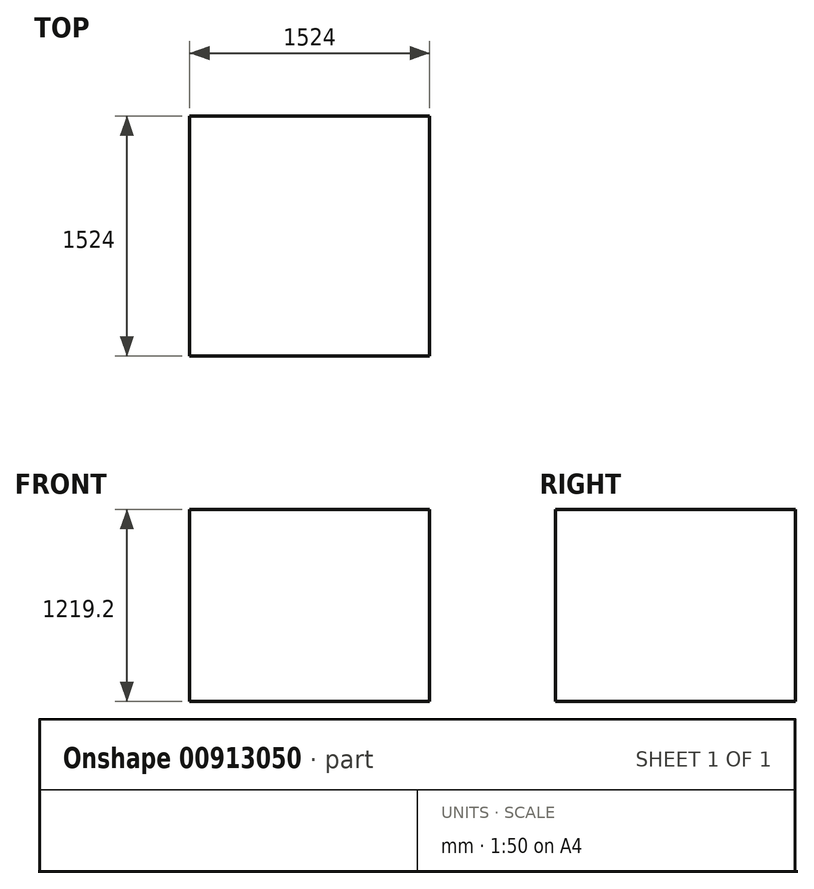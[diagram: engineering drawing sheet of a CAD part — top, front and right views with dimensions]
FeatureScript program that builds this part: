
annotation { "Feature Type Name" : "Feature", "Feature Type Description" : "" }
export const myFeature = defineFeature(function(context is Context, id is Id, definition is map)
    precondition{}
    {
        {
            var Q0;
            Q0=qCreatedBy(makeId("Top.planeOp"),FACE);
            var sketch = newSketch(context, id + "F0", { "sketchPlane" : qUnion([Q0])});
            skLineSegment(sketch, "E0.bottom", {"start": v(762, -762) * mm, "end": v(-762, -762) * mm});
            skLineSegment(sketch, "E0.top", {"start": v(762, 762) * mm, "end": v(-762, 762) * mm});
            skLineSegment(sketch, "E0.left", {"start": v(762, -762) * mm, "end": v(762, 762) * mm});
            skLineSegment(sketch, "E0.right", {"start": v(-762, -762) * mm, "end": v(-762, 762) * mm});
            skPoint(sketch, "E0.middle", {"position": v(0, 0) * mm});
            skSolve(sketch);
        }
        {
            var Q0;
            Q0=makeQuery(id+"F0.imprint","IMPRINT",FACE,{"disambiguationData":[TD([[makeQuery(id+"F0.imprint","IMPRINT",EDGE,{"derivedFrom":sQuery(id+"F0.wireOp",EDGE,"E0.bottom")}),-1.0]])]});
            extrude(context, id + "F1", {"entities" : qUnion([Q0]), "depth" : 1219.2 * mm, "offsetDistance" : 25.4 * mm});
        }
    });
